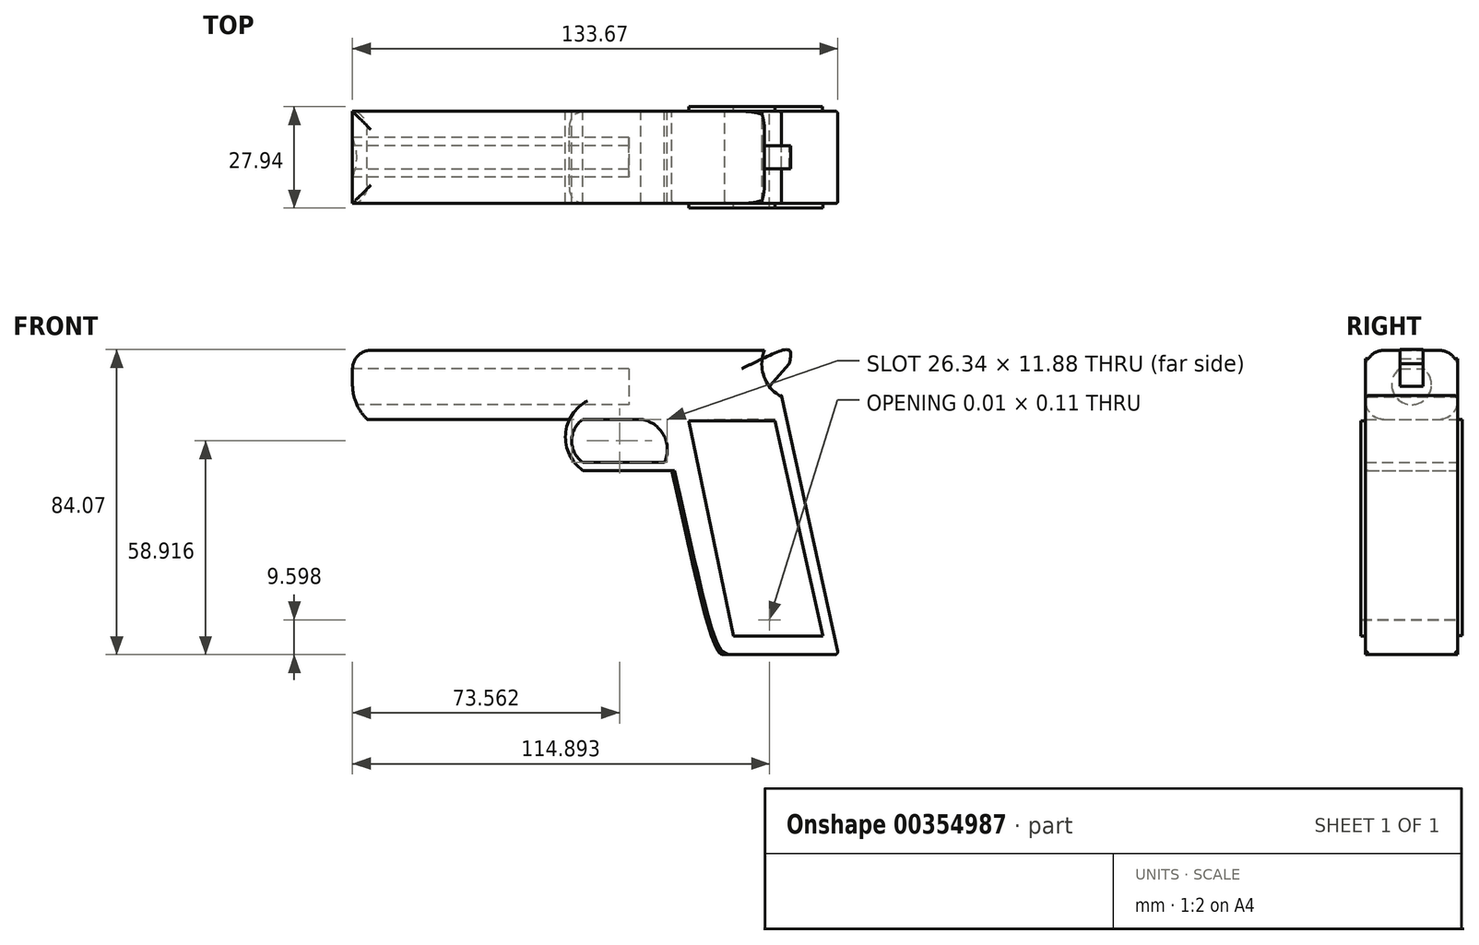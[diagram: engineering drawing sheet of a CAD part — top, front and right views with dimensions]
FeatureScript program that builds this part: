
annotation { "Feature Type Name" : "Feature", "Feature Type Description" : "" }
export const myFeature = defineFeature(function(context is Context, id is Id, definition is map)
    precondition{}
    {
        {
            var Q0;
            Q0=qCreatedBy(makeId("Front.planeOp"),FACE);
            var sketch = newSketch(context, id + "F0", { "sketchPlane" : qUnion([Q0])});
            skLineSegment(sketch, "E0", {"start": v(11.56, 44.44) * mm, "end": v(50.02, 44.44) * mm});
            skArc(sketch, "E1", {"start": v(50.02, 44.44) * mm, "mid": v(49.94, 37.16) * mm, "end": v(54.7, 31.64) * mm});
            skLineSegment(sketch, "E2", {"start": v(54.7, 32.02) * mm, "end": v(54.7, 31.64) * mm});
            skFitSpline(sketch, "E3", {"points": [v(54.7, 32.02) * mm, v(51.42, 10.8) * mm, v(51.42, -29.78) * mm, v(51.32, -18.43) * mm], "startDerivative": vector(-37, -16.06) * mm, "endDerivative": vector(-1.23, 19.06) * mm});
            skLineSegment(sketch, "E4", {"start": v(51.43, -29.78) * mm, "end": v(51.42, -29.78) * mm});
            skLineSegment(sketch, "E5", {"start": v(24.52, 11.33) * mm, "end": v(24.52, 16.48) * mm});
            skLineSegment(sketch, "E6", {"start": v(24.52, 16.48) * mm, "end": v(22.46, 13.55) * mm});
            skLineSegment(sketch, "E7", {"start": v(6.1, 44.44) * mm, "end": v(-63.47, 44.44) * mm});
            skLineSegment(sketch, "E8", {"start": v(-63.47, 44.44) * mm, "end": v(-63.47, 34.96) * mm});
            skLineSegment(sketch, "E9", {"start": v(-6.97, 25.42) * mm, "end": v(22.46, 25.42) * mm});
            skArc(sketch, "E10", {"start": v(24.52, 16.48) * mm, "mid": v(27.05, 21.77) * mm, "end": v(22.46, 25.42) * mm});
            skLineSegment(sketch, "E11", {"start": v(22.46, 13.55) * mm, "end": v(0, 13.55) * mm});
            skArc(sketch, "E12", {"start": v(0, 25.42) * mm, "mid": v(-3.08, 19.49) * mm, "end": v(0, 13.55) * mm});
            skLineSegment(sketch, "E13", {"start": v(-6.97, 25.42) * mm, "end": v(-59.42, 25.42) * mm});
            skArc(sketch, "E14", {"start": v(-63.47, 34.96) * mm, "mid": v(-62.41, 29.78) * mm, "end": v(-59.42, 25.42) * mm});
            skLineSegment(sketch, "E15", {"start": v(6.1, 44.44) * mm, "end": v(11.56, 44.44) * mm});
            skLineSegment(sketch, "E16", {"start": v(62.37, 43.15) * mm, "end": v(62.32, 43.1) * mm});
            skPoint(sketch, "E17.1.internal.snap0", {"position": v(30.79, 44.44) * mm});
            skFitSpline(sketch, "E17", {"points": [v(49.41, 42.1) * mm, v(56.85, 44.44) * mm, v(56.85, 40.7) * mm], "startDerivative": vector(16.3, 7.85) * mm, "endDerivative": vector(-2.58, -11.84) * mm});
            skLineSegment(sketch, "E18", {"start": v(56.85, 40.7) * mm, "end": v(51.39, 34.5) * mm});
            skLineSegment(sketch, "E19", {"start": v(0, 11.33) * mm, "end": v(24.52, 11.33) * mm});
            skArc(sketch, "E20", {"start": v(-3.67, 25.42) * mm, "mid": v(-4.43, 17.7) * mm, "end": v(0, 11.33) * mm});
            skArc(sketch, "E21", {"start": v(22.46, 13.55) * mm, "mid": v(22.24, 21.15) * mm, "end": v(15.94, 25.42) * mm});
            skFitSpline(sketch, "E22", {"points": [v(54.7, 32.02) * mm, v(54.7, 26.17) * mm], "startDerivative": vector(0, -5.85) * mm, "endDerivative": vector(0, -5.85) * mm});
            skPoint(sketch, "E23.visualSharp", {"position": v(70.36, -28.62) * mm});
            skArc(sketch, "E23.filletArc", {"start": v(70.26, -28.62) * mm, "mid": v(70.32, -28.59) * mm, "end": v(70.33, -28.52) * mm});
            skFitSpline(sketch, "E24", {"points": [v(24.52, 11.33) * mm, v(37.96, -39.15) * mm, v(39.06, -39.43) * mm], "startDerivative": vector(18.21, -80.01) * mm, "endDerivative": vector(4.03, -3.94) * mm});
            skLineSegment(sketch, "E25", {"start": v(39.06, -39.43) * mm, "end": v(70.38, -39.43) * mm});
            skLineSegment(sketch, "E26", {"start": v(54.7, 32.02) * mm, "end": v(70.38, -39.43) * mm});
            skSolve(sketch);
        }
        {
            var Q0;
            {var subQ9=sQuery(id+"F0.wireOp",EDGE,"E0");Q0=makeQuery(id+"F0.imprint","IMPRINT",FACE,{"disambiguationData":[TD([[makeQuery(id+"F0.imprint","IMPRINT",EDGE,{"derivedFrom":subQ9}),-1.0]])]});}
            var Q1;
            {var subQ0=sQuery(id+"F0.wireOp",EDGE,"E17");Q1=makeQuery(id+"F0.imprint","IMPRINT",FACE,{"disambiguationData":[TD([[makeQuery(id+"F0.imprint","IMPRINT",EDGE,{"derivedFrom":subQ0}),-1.0]])]});}
            var Q2;
            Q2=makeQuery(id+"F0.imprint","IMPRINT",FACE,{"disambiguationData":[TD([[makeQuery(id+"F0.imprint","IMPRINT",EDGE,{"derivedFrom":sQuery(id+"F0.wireOp",EDGE,"E6")}),-1.0]])]});
            var Q3;
            {var subQ0=sQuery(id+"F0.wireOp",EDGE,"E6");Q3=makeQuery(id+"F0.imprint","IMPRINT",FACE,{"disambiguationData":[TD([[makeQuery(id+"F0.imprint","IMPRINT",EDGE,{"derivedFrom":subQ0}),1.0]])]});}
            extrude(context, id + "F1", {"entities" : qUnion([Q0, Q1, Q2, Q3]), "depth" : 25.4 * mm});
        }
        {
            var Q0;
            Q0=makeQuery(id+"F1.opExtrude","CAP_EDGE",EDGE,{"disambiguationData":[OSD([sQuery(id+"F0.wireOp",EDGE,"E0"),sQuery(id+"F0.wireOp",EDGE,"E7"),sQuery(id+"F0.wireOp",EDGE,"E15")])],"isStart":false});
            var Q1;
            Q1=makeQuery(id+"F1.opExtrude","CAP_EDGE",EDGE,{"disambiguationData":[OSD([sQuery(id+"F0.wireOp",EDGE,"E0"),sQuery(id+"F0.wireOp",EDGE,"E7"),sQuery(id+"F0.wireOp",EDGE,"E15")])],"isStart":true});
            var Q2;
            Q2=makeQuery(id+"F1.opExtrude","SWEPT_EDGE",EDGE,{"disambiguationData":[OSD([sQuery(id+"F0.wireOp",EDGE,"E7"),sQuery(id+"F0.wireOp",EDGE,"E8")])]});
            var Q3;
            Q3=makeQuery(id+"F1.opExtrude","CAP_EDGE",EDGE,{"disambiguationData":[OSD([sQuery(id+"F0.wireOp",EDGE,"E9"),sQuery(id+"F0.wireOp",EDGE,"E13")])],"isStart":false});
            var Q4;
            Q4=makeQuery(id+"F1.opExtrude","CAP_EDGE",EDGE,{"disambiguationData":[OSD([sQuery(id+"F0.wireOp",EDGE,"E9"),sQuery(id+"F0.wireOp",EDGE,"E13")])],"isStart":true});
            fillet(context, id + "F2", {"entities" : qUnion([Q0, Q1, Q2, Q3, Q4]), "radius" : 5.08 * mm, "tangentPropagation" : true, "allowEdgeOverflow" : false});
        }
        {
            var Q0;
            Q0=makeQuery(id+"F1.opExtrude","CAP_FACE",FACE,{"disambiguationData":[OSD([sQuery(id+"F0.wireOp",EDGE,"E0"),sQuery(id+"F0.wireOp",EDGE,"E1"),sQuery(id+"F0.wireOp",EDGE,"E3"),sQuery(id+"F0.wireOp",EDGE,"ETqB8So8-rKZg-N5FO-pKHe-pVmDtdDpMhgb"),sQuery(id+"F0.wireOp",EDGE,"E5"),sQuery(id+"F0.wireOp",EDGE,"E7"),sQuery(id+"F0.wireOp",EDGE,"E8"),sQuery(id+"F0.wireOp",EDGE,"E9"),sQuery(id+"F0.wireOp",EDGE,"2GhQpJlp-mDSz-t7D7-0lNr-Fk9lNn3einf8"),sQuery(id+"F0.wireOp",EDGE,"E11"),sQuery(id+"F0.wireOp",EDGE,"E12"),sQuery(id+"F0.wireOp",EDGE,"E13"),sQuery(id+"F0.wireOp",EDGE,"E14"),sQuery(id+"F0.wireOp",EDGE,"E15"),sQuery(id+"F0.wireOp",EDGE,"E17"),sQuery(id+"F0.wireOp",EDGE,"E18"),sQuery(id+"F0.wireOp",EDGE,"E19"),sQuery(id+"F0.wireOp",EDGE,"E20")])],"isStart":false});
            var sketch = newSketch(context, id + "F3", { "sketchPlane" : qUnion([Q0])});
            skLineSegment(sketch, "E27", {"start": v(1.26, 30.5) * mm, "end": v(18.17, 30.5) * mm});
            skLineSegment(sketch, "E28", {"start": v(24.52, 24.15) * mm, "end": v(24.52, 11.33) * mm});
            skPoint(sketch, "E29.visualSharp", {"position": v(24.52, 30.5) * mm});
            skArc(sketch, "E29.filletArc", {"start": v(24.52, 24.15) * mm, "mid": v(22.66, 28.64) * mm, "end": v(18.17, 30.5) * mm});
            skLineSegment(sketch, "E30", {"start": v(18.17, 30.5) * mm, "end": v(54.7, 31.64) * mm});
            skLineSegment(sketch, "E31", {"start": v(35.2, 31.03) * mm, "end": v(35.2, 32.02) * mm});
            skPoint(sketch, "E32.end.orphan", {"position": v(54.7, 32.02) * mm});
            skFitSpline(sketch, "E33", {"points": [v(29.18, 24.97) * mm, v(41.5, -34.3) * mm], "startDerivative": vector(12.33, -59.26) * mm, "endDerivative": vector(12.33, -59.26) * mm});
            skFitSpline(sketch, "E34", {"points": [v(52.94, 24.97) * mm, v(66.17, -34.3) * mm], "startDerivative": vector(13.23, -59.26) * mm, "endDerivative": vector(13.23, -59.26) * mm});
            skLineSegment(sketch, "E35", {"start": v(29.18, 24.97) * mm, "end": v(52.94, 24.97) * mm});
            skLineSegment(sketch, "E36", {"start": v(41.5, -34.3) * mm, "end": v(66.17, -34.3) * mm});
            skSolve(sketch);
        }
        {
            var Q0;
            Q0=makeQuery(id+"F3.imprint","IMPRINT",FACE,{"disambiguationData":[TD([[makeQuery(id+"F3.imprint","IMPRINT",EDGE,{"derivedFrom":sQuery(id+"F3.wireOp",EDGE,"SnrBnyyG-mVTW-nTGt-GneA-SuEm3iO1Mqjh")}),1.0]])]});
            var Q1;
            Q1=makeQuery(id+"F3.imprint","IMPRINT",FACE,{"disambiguationData":[TD([[makeQuery(id+"F3.imprint","IMPRINT",EDGE,{"derivedFrom":sQuery(id+"F3.wireOp",EDGE,"E33")}),1.0]])]});
            extrude(context, id + "F4", {"entities" : qUnion([Q0, Q1]), "operationType" : NewBodyOperationType.ADD, "depth" : 1.27 * mm});
        }
        {
            var Q0;
            Q0=makeQuery(id+"F1.opExtrude","CAP_FACE",FACE,{"disambiguationData":[OSD([sQuery(id+"F0.wireOp",EDGE,"E0"),sQuery(id+"F0.wireOp",EDGE,"E1"),sQuery(id+"F0.wireOp",EDGE,"E3"),sQuery(id+"F0.wireOp",EDGE,"ETqB8So8-rKZg-N5FO-pKHe-pVmDtdDpMhgb"),sQuery(id+"F0.wireOp",EDGE,"E5"),sQuery(id+"F0.wireOp",EDGE,"E7"),sQuery(id+"F0.wireOp",EDGE,"E8"),sQuery(id+"F0.wireOp",EDGE,"E9"),sQuery(id+"F0.wireOp",EDGE,"2GhQpJlp-mDSz-t7D7-0lNr-Fk9lNn3einf8"),sQuery(id+"F0.wireOp",EDGE,"E11"),sQuery(id+"F0.wireOp",EDGE,"E12"),sQuery(id+"F0.wireOp",EDGE,"E13"),sQuery(id+"F0.wireOp",EDGE,"E14"),sQuery(id+"F0.wireOp",EDGE,"E15"),sQuery(id+"F0.wireOp",EDGE,"E17"),sQuery(id+"F0.wireOp",EDGE,"E18"),sQuery(id+"F0.wireOp",EDGE,"E19"),sQuery(id+"F0.wireOp",EDGE,"E20")])],"isStart":true});
            var sketch = newSketch(context, id + "F5", { "sketchPlane" : qUnion([Q0])});
            skLineSegment(sketch, "E37", {"start": v(-1.26, 30.5) * mm, "end": v(-54.7, 30.5) * mm});
            skPoint(sketch, "E38.endSnap0", {"position": v(-11.23, 13.55) * mm});
            skLineSegment(sketch, "E39", {"start": v(-29.24, 25.15) * mm, "end": v(-41.4, -34.23) * mm});
            skLineSegment(sketch, "E40", {"start": v(-41.4, -34.23) * mm, "end": v(-66.07, -34.23) * mm});
            skLineSegment(sketch, "E41", {"start": v(-66.07, -34.23) * mm, "end": v(-52.96, 25.42) * mm});
            skLineSegment(sketch, "E42", {"start": v(-52.96, 25.42) * mm, "end": v(-29.24, 25.15) * mm});
            skSolve(sketch);
        }
        {
            var Q0;
            Q0=makeQuery(id+"F5.imprint","IMPRINT",FACE,{"disambiguationData":[TD([[makeQuery(id+"F5.imprint","IMPRINT",EDGE,{"derivedFrom":sQuery(id+"F5.wireOp",EDGE,"XWZJYSIO-3UBe-8zMu-2IkU-z2B4XycWp5tm")}),-1.0]])]});
            var Q1;
            Q1=makeQuery(id+"F5.imprint","IMPRINT",FACE,{"disambiguationData":[TD([[makeQuery(id+"F5.imprint","IMPRINT",EDGE,{"derivedFrom":sQuery(id+"F5.wireOp",EDGE,"E39")}),-1.0]])]});
            extrude(context, id + "F6", {"entities" : qUnion([Q0, Q1]), "operationType" : NewBodyOperationType.ADD, "depth" : 1.27 * mm});
        }
        {
            var Q0;
            Q0=makeQuery(id+"F1.opExtrude","CAP_EDGE",EDGE,{"disambiguationData":[OSD([sQuery(id+"F0.wireOp",EDGE,"ETqB8So8-rKZg-N5FO-pKHe-pVmDtdDpMhgb")])],"isStart":false});
            var Q1;
            Q1=makeQuery(id+"F1.opExtrude","CAP_EDGE",EDGE,{"disambiguationData":[OSD([sQuery(id+"F0.wireOp",EDGE,"ETqB8So8-rKZg-N5FO-pKHe-pVmDtdDpMhgb")])],"isStart":true});
            var Q2;
            Q2=makeQuery(id+"F1.opExtrude","SWEPT_EDGE",EDGE,{"disambiguationData":[OSD([sQuery(id+"F0.wireOp",EDGE,"E25"),sQuery(id+"F0.wireOp",EDGE,"E26")])]});
            var Q3;
            Q3=makeQuery(id+"F1.opExtrude","CAP_EDGE",EDGE,{"disambiguationData":[OSD([sQuery(id+"F0.wireOp",EDGE,"E24")])],"isStart":false});
            var Q4;
            Q4=makeQuery(id+"F1.opExtrude","CAP_EDGE",EDGE,{"disambiguationData":[OSD([sQuery(id+"F0.wireOp",EDGE,"E26")])],"isStart":false});
            var Q5;
            Q5=makeQuery(id+"F1.opExtrude","CAP_EDGE",EDGE,{"disambiguationData":[OSD([sQuery(id+"F0.wireOp",EDGE,"E26")])],"isStart":true});
            fillet(context, id + "F7", {"entities" : qUnion([Q0, Q1, Q2, Q3, Q4, Q5]), "radius" : 0.76 * mm, "tangentPropagation" : true, "allowEdgeOverflow" : false});
        }
        {
            var Q0;
            {var subQ0=sQuery(id+"F0.wireOp",EDGE,"E17");Q0=makeQuery(id+"F0.imprint","IMPRINT",FACE,{"disambiguationData":[TD([[makeQuery(id+"F0.imprint","IMPRINT",EDGE,{"derivedFrom":subQ0}),-1.0]])]});}
            extrude(context, id + "F8", {"entities" : qUnion([Q0]), "operationType" : NewBodyOperationType.ADD, "depth" : 12.7 * mm});
        }
        {
            var Q0;
            {var subQ0=sQuery(id+"F0.wireOp",EDGE,"E17");Q0=makeQuery(id+"F0.imprint","IMPRINT",FACE,{"disambiguationData":[TD([[makeQuery(id+"F0.imprint","IMPRINT",EDGE,{"derivedFrom":subQ0}),-1.0]])]});}
            extrude(context, id + "F9", {"entities" : qUnion([Q0]), "operationType" : NewBodyOperationType.REMOVE, "depth" : 9.52 * mm, "hasSecondDirection" : true, "secondDirectionOppositeDirection" : true, "secondDirectionDepth" : 25.4 * mm});
        }
        {
            var Q0;
            {var subQ0=sQuery(id+"F0.wireOp",EDGE,"E17");Q0=makeQuery(id+"F0.imprint","IMPRINT",FACE,{"disambiguationData":[TD([[makeQuery(id+"F0.imprint","IMPRINT",EDGE,{"derivedFrom":subQ0}),-1.0]])]});}
            extrude(context, id + "F10", {"entities" : qUnion([Q0]), "operationType" : NewBodyOperationType.REMOVE, "depth" : 44.96 * mm, "hasSecondDirection" : true, "secondDirectionOppositeDirection" : false, "secondDirectionDepth" : 25.4 * mm});
        }
        {
            var Q0;
            Q0=makeQuery(id+"F1.opExtrude","SWEPT_FACE",FACE,{"disambiguationData":[OSD([sQuery(id+"F0.wireOp",EDGE,"E8")])]});
            var sketch = newSketch(context, id + "F11", { "sketchPlane" : qUnion([Q0])});
            skCircle(sketch, "E43", {"center": v(12.7, 34.96) * mm, "radius": 5.49 * mm});
            skSolve(sketch);
        }
        {
            var Q0;
            {var subQ0=sQuery(id+"F11.wireOp",EDGE,"E43");var subQ1=sQuery(id+"F0.wireOp",EDGE,"E8");var subQ2=makeQuery(id+"F2.opFillet","BLEND_EDGE",EDGE,{"blendedFrom":[makeQuery(id+"F1.opExtrude","SWEPT_EDGE",EDGE,{"disambiguationData":[OSD([sQuery(id+"F0.wireOp",EDGE,"E7"),subQ1])]}),makeQuery(id+"F1.opExtrude","SWEPT_FACE",FACE,{"disambiguationData":[OSD([subQ1])]})],"blendedInto":[makeQuery(id+"F1.opExtrude","SWEPT_FACE",FACE,{"disambiguationData":[OSD([subQ1])]})]});var subQ3=makeQuery(id+"F11.imprint","INTERSECT",VERTEX,{"disambiguationData":[OD(0.0)],"derivedFrom":[subQ2,subQ0]});Q0=makeQuery(id+"F11.imprint","IMPRINT",FACE,{"disambiguationData":[TD([[makeQuery(id+"F11.imprint","IMPRINT",EDGE,{"disambiguationData":[TD([[subQ3,-1.0]])],"derivedFrom":subQ0}),1.0]])]});}
            var Q1;
            {var subQ0=sQuery(id+"F11.wireOp",EDGE,"E43");var subQ1=sQuery(id+"F0.wireOp",EDGE,"E8");var subQ4=makeQuery(id+"F1.opExtrude","SWEPT_EDGE",EDGE,{"disambiguationData":[OSD([subQ1,sQuery(id+"F0.wireOp",EDGE,"E14")])]});var subQ5=makeQuery(id+"F11.imprint","INTERSECT",VERTEX,{"disambiguationData":[OD(0.0)],"derivedFrom":[subQ4,subQ0]});Q1=makeQuery(id+"F11.imprint","IMPRINT",FACE,{"disambiguationData":[TD([[makeQuery(id+"F11.imprint","IMPRINT",EDGE,{"disambiguationData":[TD([[subQ5,-1.0]])],"derivedFrom":subQ0}),1.0]])]});}
            var Q2;
            {var subQ0=sQuery(id+"F11.wireOp",EDGE,"E43");var subQ1=makeQuery(id+"F1.opExtrude","SWEPT_EDGE",EDGE,{"disambiguationData":[OSD([sQuery(id+"F0.wireOp",EDGE,"E8"),sQuery(id+"F0.wireOp",EDGE,"E14")])]});var subQ2=makeQuery(id+"F11.imprint","INTERSECT",VERTEX,{"disambiguationData":[OD(0.0)],"derivedFrom":[subQ1,subQ0]});Q2=makeQuery(id+"F11.imprint","IMPRINT",FACE,{"disambiguationData":[TD([[makeQuery(id+"F11.imprint","IMPRINT",EDGE,{"disambiguationData":[TD([[subQ2,1.0]])],"derivedFrom":subQ0}),1.0]])]});}
            extrude(context, id + "F12", {"entities" : qUnion([Q0, Q1, Q2]), "operationType" : NewBodyOperationType.REMOVE, "oppositeDirection" : true, "depth" : 76.2 * mm});
        }
        {
            var Q0;
            {var subQ0=sQuery(id+"F0.wireOp",EDGE,"E17");Q0=makeQuery(id+"F0.imprint","IMPRINT",FACE,{"disambiguationData":[TD([[makeQuery(id+"F0.imprint","IMPRINT",EDGE,{"derivedFrom":subQ0}),-1.0]])]});}
            extrude(context, id + "F13", {"entities" : qUnion([Q0]), "operationType" : NewBodyOperationType.REMOVE, "depth" : 25.4 * mm, "hasSecondDirection" : true, "secondDirectionOppositeDirection" : false, "secondDirectionDepth" : 15.88 * mm});
        }
    });
